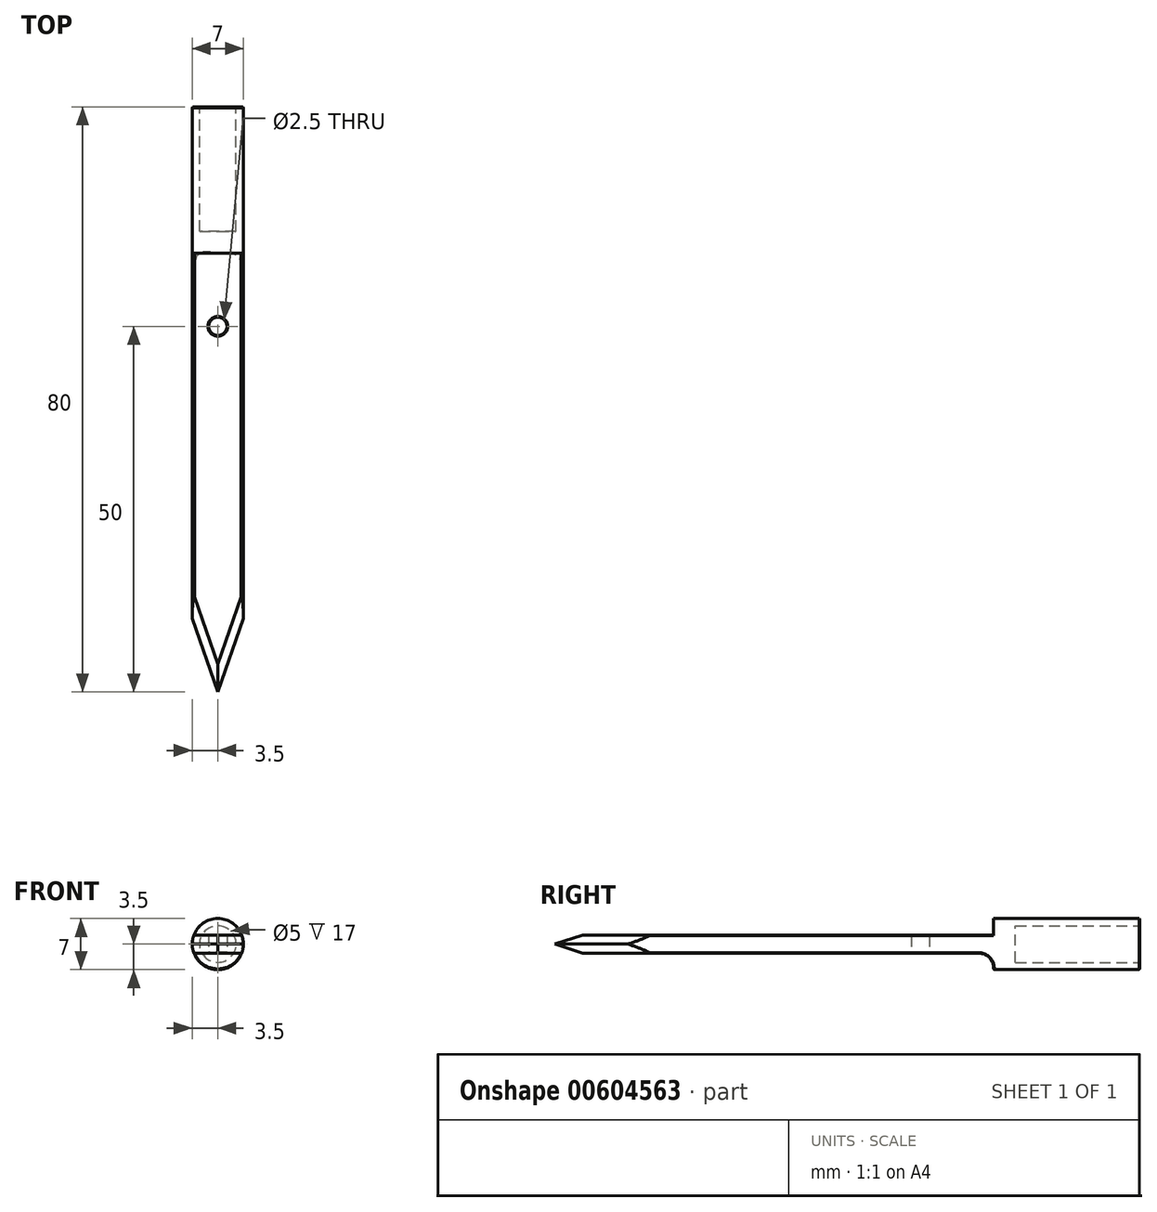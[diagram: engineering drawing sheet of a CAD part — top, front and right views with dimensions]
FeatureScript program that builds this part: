
annotation { "Feature Type Name" : "Feature", "Feature Type Description" : "" }
export const myFeature = defineFeature(function(context is Context, id is Id, definition is map)
    precondition{}
    {
        {
            var Q0;
            Q0=qCreatedBy(makeId("Top.planeOp"),FACE);
            var sketch = newSketch(context, id + "F0", { "sketchPlane" : qUnion([Q0])});
            skLineSegment(sketch, "E0.bottom", {"start": v(-3.5, 25) * mm, "end": v(3.5, 25) * mm});
            skLineSegment(sketch, "E0.left", {"start": v(-3.5, 25) * mm, "end": v(-3.5, -25) * mm});
            skLineSegment(sketch, "E0.right", {"start": v(3.5, 25) * mm, "end": v(3.5, -25) * mm});
            skLineSegment(sketch, "E1", {"start": v(-3.5, -25) * mm, "end": v(0, -35) * mm});
            skLineSegment(sketch, "E2", {"start": v(0, -35) * mm, "end": v(3.5, -25) * mm});
            skCircle(sketch, "E3", {"center": v(0, 15) * mm, "radius": 1.25 * mm});
            skSolve(sketch);
        }
        {
            var Q0;
            Q0 = qSketchRegion(id + "F0", true);
            extrude(context, id + "F1", {"entities" : qUnion([Q0]), "depth" : 2.5 * mm, "offsetDistance" : 25 * mm});
        }
        {
            var Q0;
            Q0=makeQuery(id+"F1.opExtrude","CAP_EDGE",EDGE,{"disambiguationData":[OSD([sQuery(id+"F0.wireOp",EDGE,"E2")])],"isStart":false});
            var Q1;
            Q1=makeQuery(id+"F1.opExtrude","CAP_EDGE",EDGE,{"disambiguationData":[OSD([sQuery(id+"F0.wireOp",EDGE,"E1")])],"isStart":false});
            var Q2;
            Q2=makeQuery(id+"F1.opExtrude","CAP_EDGE",EDGE,{"disambiguationData":[OSD([sQuery(id+"F0.wireOp",EDGE,"E1")])],"isStart":true});
            var Q3;
            Q3=makeQuery(id+"F1.opExtrude","CAP_EDGE",EDGE,{"disambiguationData":[OSD([sQuery(id+"F0.wireOp",EDGE,"E2")])],"isStart":true});
            chamfer(context, id + "F2", {"entities" : qUnion([Q0, Q1, Q2, Q3]), "width" : 1.25 * mm, "tangentPropagation" : true});
        }
        {
            var Q0;
            Q0=qCreatedBy(makeId("Front.planeOp"),FACE);
            cPlane(context, id + "F3", {"entities" : qUnion([Q0]), "cplaneType" : CPlaneType.OFFSET, "offset" : 25 * mm, "oppositeDirection" : true, "width" : 150 * mm, "height" : 150 * mm});
        }
        {
            var Q0;
            Q0=qCreatedBy(id+"F3.planeOp",FACE);
            var sketch = newSketch(context, id + "F4", { "sketchPlane" : qUnion([Q0])});
            skCircle(sketch, "E4", {"center": v(0, 1.25) * mm, "radius": 3.5 * mm});
            skSolve(sketch);
        }
        {
            var Q0;
            Q0=makeQuery(id+"F4.imprint","IMPRINT",FACE,{"disambiguationData":[TD([[makeQuery(id+"F4.imprint","IMPRINT",EDGE,{"derivedFrom":sQuery(id+"F4.wireOp",EDGE,"E4")}),1.0]])]});
            extrude(context, id + "F5", {"entities" : qUnion([Q0]), "operationType" : NewBodyOperationType.ADD, "oppositeDirection" : true, "depth" : 20 * mm, "offsetDistance" : 25 * mm});
        }
        {
            var Q0;
            Q0=qCreatedBy(id+"F3.planeOp",FACE);
            var sketch = newSketch(context, id + "F6", { "sketchPlane" : qUnion([Q0])});
            skCircle(sketch, "E5", {"center": v(0, 1.25) * mm, "radius": 3.5 * mm});
            skCircle(sketch, "E6", {"center": v(0, 1.25) * mm, "radius": 5.3 * mm});
            skSolve(sketch);
        }
        {
            var Q0;
            Q0=makeQuery(id+"F6.imprint","IMPRINT",FACE,{"disambiguationData":[TD([[makeQuery(id+"F6.imprint","IMPRINT",EDGE,{"derivedFrom":sQuery(id+"F6.wireOp",EDGE,"E5")}),-1.0]])]});
            extrude(context, id + "F7", {"entities" : qUnion([Q0]), "operationType" : NewBodyOperationType.REMOVE, "depth" : 60 * mm, "offsetDistance" : 25 * mm});
        }
        {
            var Q0;
            Q0=qCreatedBy(id+"F3.planeOp",FACE);
            cPlane(context, id + "F8", {"entities" : qUnion([Q0]), "cplaneType" : CPlaneType.OFFSET, "offset" : 20 * mm, "oppositeDirection" : true, "width" : 150 * mm, "height" : 150 * mm});
        }
        {
            var Q0;
            Q0=qCreatedBy(id+"F8.planeOp",FACE);
            var sketch = newSketch(context, id + "F9", { "sketchPlane" : qUnion([Q0])});
            skCircle(sketch, "E7", {"center": v(0, 1.25) * mm, "radius": 2.5 * mm});
            skSolve(sketch);
        }
        {
            var Q0;
            Q0=makeQuery(id+"F9.imprint","IMPRINT",FACE,{"disambiguationData":[TD([[makeQuery(id+"F9.imprint","IMPRINT",EDGE,{"derivedFrom":sQuery(id+"F9.wireOp",EDGE,"E7")}),1.0]])]});
            extrude(context, id + "F10", {"entities" : qUnion([Q0]), "operationType" : NewBodyOperationType.REMOVE, "depth" : 17 * mm, "offsetDistance" : 25 * mm});
        }
        {
            var Q0;
            {var subQ0=sQuery(id+"F0.wireOp",EDGE,"E0.bottom");Q0=makeQuery(id+"F5.boolean.opBoolean","SPLIT",EDGE,{"disambiguationData":[topologyDisambiguationEdgeConnected([makeQuery(id+"F1.opExtrude","CAP_FACE",FACE,{"disambiguationData":[OSD([subQ0,sQuery(id+"F0.wireOp",EDGE,"E0.left"),sQuery(id+"F0.wireOp",EDGE,"E0.right"),sQuery(id+"F0.wireOp",EDGE,"E1"),sQuery(id+"F0.wireOp",EDGE,"E2"),sQuery(id+"F0.wireOp",EDGE,"E3")])],"isStart":false}),makeQuery(id+"F5.opExtrude","CAP_FACE",FACE,{"disambiguationData":[OSD([sQuery(id+"F4.wireOp",EDGE,"E4")])],"isStart":true})])],"derivedFrom":makeQuery(id+"F1.opExtrude","CAP_EDGE",EDGE,{"disambiguationData":[OSD([subQ0])],"isStart":false})});}
            var Q1;
            {var subQ0=sQuery(id+"F0.wireOp",EDGE,"E0.bottom");Q1=makeQuery(id+"F5.boolean.opBoolean","SPLIT",EDGE,{"disambiguationData":[topologyDisambiguationEdgeConnected([makeQuery(id+"F1.opExtrude","CAP_FACE",FACE,{"disambiguationData":[OSD([subQ0,sQuery(id+"F0.wireOp",EDGE,"E0.left"),sQuery(id+"F0.wireOp",EDGE,"E0.right"),sQuery(id+"F0.wireOp",EDGE,"E1"),sQuery(id+"F0.wireOp",EDGE,"E2"),sQuery(id+"F0.wireOp",EDGE,"E3")])],"isStart":true}),makeQuery(id+"F5.opExtrude","CAP_FACE",FACE,{"disambiguationData":[OSD([sQuery(id+"F4.wireOp",EDGE,"E4")])],"isStart":true})])],"derivedFrom":makeQuery(id+"F1.opExtrude","CAP_EDGE",EDGE,{"disambiguationData":[OSD([subQ0])],"isStart":true})});}
            fillet(context, id + "F11", {"entities" : qUnion([Q0, Q1]), "radius" : 2 * mm, "tangentPropagation" : true, "allowEdgeOverflow" : false});
        }
        {
            var Q0;
            Q0=makeQuery(id+"F5.opExtrude","CAP_EDGE",EDGE,{"disambiguationData":[OSD([sQuery(id+"F4.wireOp",EDGE,"E4")])],"isStart":false});
            var Q1;
            Q1=makeQuery(id+"F10.boolean.opBoolean","COPY",EDGE,{"derivedFrom":makeQuery(id+"F10.opExtrude","CAP_EDGE",EDGE,{"disambiguationData":[OSD([sQuery(id+"F9.wireOp",EDGE,"E7")])],"isStart":true})});
            var Q2;
            Q2=makeQuery(id+"F1.opExtrude","CAP_EDGE",EDGE,{"disambiguationData":[OSD([sQuery(id+"F0.wireOp",EDGE,"E3")])],"isStart":false});
            var Q3;
            Q3=makeQuery(id+"F1.opExtrude","CAP_EDGE",EDGE,{"disambiguationData":[OSD([sQuery(id+"F0.wireOp",EDGE,"E3")])],"isStart":true});
            var Q4;
            Q4=makeQuery(id+"F7.boolean.opBoolean","INTERSECT",EDGE,{"disambiguationData":[OD(1.0)],"derivedFrom":[makeQuery(id+"F1.opExtrude","CAP_FACE",FACE,{"disambiguationData":[OSD([sQuery(id+"F0.wireOp",EDGE,"E0.bottom"),sQuery(id+"F0.wireOp",EDGE,"E0.left"),sQuery(id+"F0.wireOp",EDGE,"E0.right"),sQuery(id+"F0.wireOp",EDGE,"E1"),sQuery(id+"F0.wireOp",EDGE,"E2"),sQuery(id+"F0.wireOp",EDGE,"E3")])],"isStart":false}),makeQuery(id+"F7.opExtrude","SWEPT_FACE",FACE,{"disambiguationData":[OSD([sQuery(id+"F6.wireOp",EDGE,"E5")])]})]});
            var Q5;
            Q5=makeQuery(id+"F7.boolean.opBoolean","INTERSECT",EDGE,{"disambiguationData":[OD(1.0)],"derivedFrom":[makeQuery(id+"F1.opExtrude","CAP_FACE",FACE,{"disambiguationData":[OSD([sQuery(id+"F0.wireOp",EDGE,"E0.bottom"),sQuery(id+"F0.wireOp",EDGE,"E0.left"),sQuery(id+"F0.wireOp",EDGE,"E0.right"),sQuery(id+"F0.wireOp",EDGE,"E1"),sQuery(id+"F0.wireOp",EDGE,"E2"),sQuery(id+"F0.wireOp",EDGE,"E3")])],"isStart":true}),makeQuery(id+"F7.opExtrude","SWEPT_FACE",FACE,{"disambiguationData":[OSD([sQuery(id+"F6.wireOp",EDGE,"E5")])]})]});
            var Q6;
            Q6=makeQuery(id+"F7.boolean.opBoolean","INTERSECT",EDGE,{"disambiguationData":[OD(0.0)],"derivedFrom":[makeQuery(id+"F1.opExtrude","CAP_FACE",FACE,{"disambiguationData":[OSD([sQuery(id+"F0.wireOp",EDGE,"E0.bottom"),sQuery(id+"F0.wireOp",EDGE,"E0.left"),sQuery(id+"F0.wireOp",EDGE,"E0.right"),sQuery(id+"F0.wireOp",EDGE,"E1"),sQuery(id+"F0.wireOp",EDGE,"E2"),sQuery(id+"F0.wireOp",EDGE,"E3")])],"isStart":false}),makeQuery(id+"F7.opExtrude","SWEPT_FACE",FACE,{"disambiguationData":[OSD([sQuery(id+"F6.wireOp",EDGE,"E5")])]})]});
            var Q7;
            Q7=makeQuery(id+"F7.boolean.opBoolean","INTERSECT",EDGE,{"disambiguationData":[OD(0.0)],"derivedFrom":[makeQuery(id+"F1.opExtrude","CAP_FACE",FACE,{"disambiguationData":[OSD([sQuery(id+"F0.wireOp",EDGE,"E0.bottom"),sQuery(id+"F0.wireOp",EDGE,"E0.left"),sQuery(id+"F0.wireOp",EDGE,"E0.right"),sQuery(id+"F0.wireOp",EDGE,"E1"),sQuery(id+"F0.wireOp",EDGE,"E2"),sQuery(id+"F0.wireOp",EDGE,"E3")])],"isStart":true}),makeQuery(id+"F7.opExtrude","SWEPT_FACE",FACE,{"disambiguationData":[OSD([sQuery(id+"F6.wireOp",EDGE,"E5")])]})]});
            chamfer(context, id + "F12", {"entities" : qUnion([Q0, Q1, Q2, Q3, Q4, Q5, Q6, Q7]), "width" : 0.1 * mm, "tangentPropagation" : true});
        }
    });
